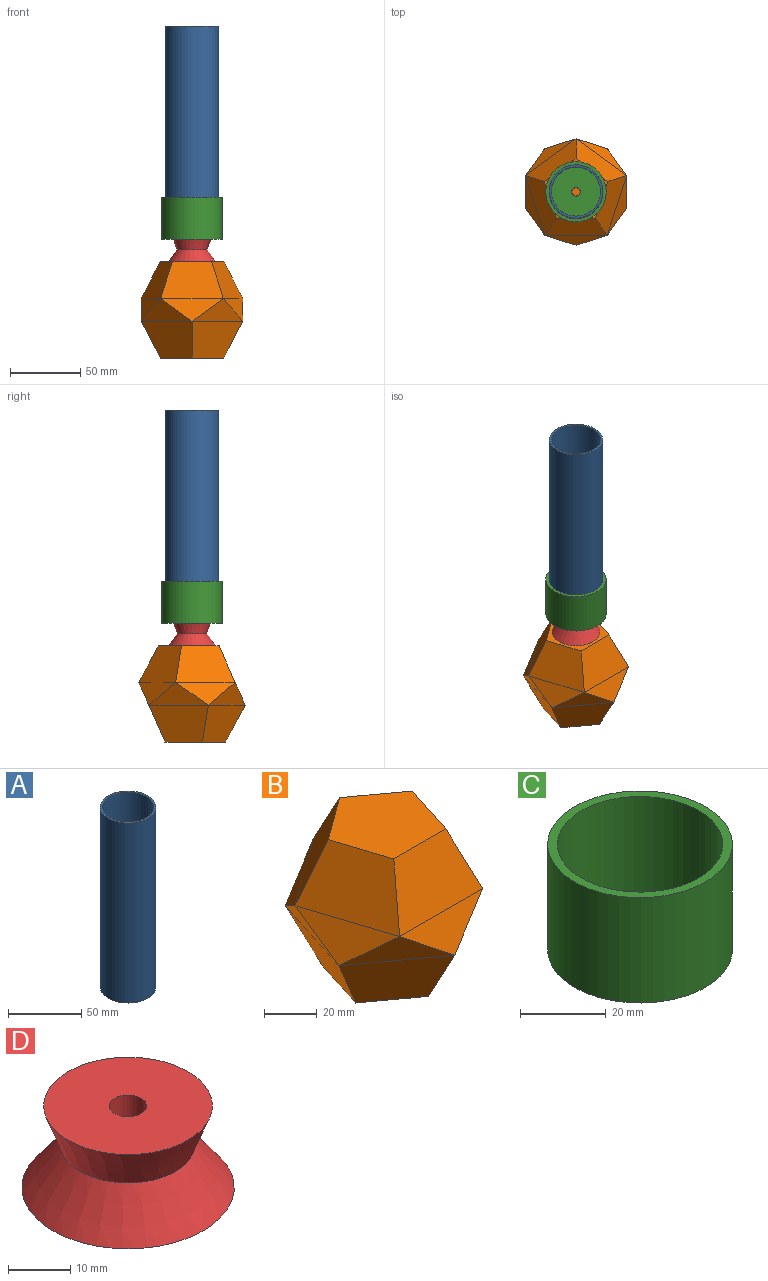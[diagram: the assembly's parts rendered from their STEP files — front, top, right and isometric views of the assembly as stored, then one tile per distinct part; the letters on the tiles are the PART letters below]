
ASSEMBLY  parts=4 mates=3
PART A: 4 faces, bbox 38x38x150 mm
  f0: cylinder r=17.5mm len=150mm, axis (0,0,-1), area 16493.4mm2, adj f2,f3
  f1: cylinder r=19mm len=150mm, axis (0,0,-1), area 17907.1mm2, adj f2,f3
  f2: plane 38x38mm, normal (0,0,1), area 172mm2, adj f0,f1
  f3: plane 38x38mm, normal (0,0,-1), area 172mm2, adj f0,f1
PART B: 22 faces, bbox 72.3x76x68.7 mm
  f0: plane 45.31x43.09mm, normal (0,0,1), area 1348.9mm2, adj f1,f2,f3,f4,f5
  f1: plane 44.66x26.25mm, normal (0,-0.92,0.4), area 1040.6mm2, adj f0,f2,f5,f7
  f2: plane 42.47x26.25mm, normal (0.87,-0.28,0.4), area 1040.6mm2, adj f0,f1,f3,f8
  f3: plane 36.13x30.63mm, normal (0.54,0.74,0.4), area 1040.6mm2, adj f0,f2,f4,f9
  f4: plane 36.13x30.63mm, normal (-0.54,0.74,0.4), area 1040.6mm2, adj f0,f3,f5,f10
  f5: plane 42.47x26.25mm, normal (-0.87,-0.28,0.4), area 1040.6mm2, adj f0,f1,f4,f6
  f6: plane 42.47x16.22mm, normal (-0.87,-0.28,0.41), area 396.8mm2, adj f5,f14,f15
  f7: plane 44.66x16.22mm, normal (0,-0.91,0.41), area 396.8mm2, adj f1,f11,f15
  f8: plane 42.47x16.22mm, normal (0.87,-0.28,0.41), area 396.8mm2, adj f2,f11,f12
  f9: plane 36.13x26.25mm, normal (0.54,0.74,0.41), area 396.8mm2, adj f3,f12,f13
  f10: plane 36.13x26.25mm, normal (-0.54,0.74,0.41), area 396.8mm2, adj f4,f13,f14
  f11: plane 36.13x26.25mm, normal (0.54,-0.74,-0.41), area 396.8mm2, adj f7,f8,f19
  f12: plane 42.47x16.22mm, normal (0.87,0.28,-0.41), area 396.8mm2, adj f8,f9,f18
  f13: plane 44.66x16.22mm, normal (0,0.91,-0.41), area 396.8mm2, adj f9,f10,f17
  f14: plane 42.47x16.22mm, normal (-0.87,0.28,-0.41), area 396.8mm2, adj f6,f10,f21
  f15: plane 36.13x26.25mm, normal (-0.54,-0.74,-0.41), area 396.8mm2, adj f6,f7,f20
  f16: plane 45.31x43.09mm, normal (0,0,-1), area 1348.9mm2, adj f17,f18,f19,f20,f21
  f17: plane 44.66x26.25mm, normal (0,0.92,-0.4), area 1040.6mm2, adj f13,f16,f18,f21
  f18: plane 42.47x26.25mm, normal (0.87,0.28,-0.4), area 1040.6mm2, adj f12,f16,f17,f19
  f19: plane 36.13x30.63mm, normal (0.54,-0.74,-0.4), area 1040.6mm2, adj f11,f16,f18,f20
  f20: plane 36.13x30.63mm, normal (-0.54,-0.74,-0.4), area 1040.6mm2, adj f15,f16,f19,f21
  f21: plane 42.47x26.25mm, normal (-0.87,0.28,-0.4), area 1040.6mm2, adj f14,f16,f17,f20
PART C: 6 faces, bbox 43x43x30 mm
  f0: plane 38.5x38.5mm, normal (0,0,1), area 1135.9mm2, adj f1,f4
  f1: cylinder r=3mm len=6mm, axis (0,0,-1), area 37.7mm2, adj f0,f3
  f2: cylinder r=21.5mm len=43mm, axis (0,0,-1), area 4052.7mm2, adj f3,f5
  f3: plane 43x43mm, normal (0,0,-1), area 1423.9mm2, adj f1,f2
  f4: cylinder r=19.25mm len=38.5mm, axis (0,0,-1), area 3386.6mm2, adj f0,f5
  f5: plane 43x43mm, normal (0,0,1), area 288mm2, adj f2,f4
PART D: 5 faces, bbox 34x34x16 mm
  f0: plane 34x34mm, normal (0,0,-1), area 879.6mm2, adj f1,f4
  f1: cone r=11mm half-angle=36.9deg, axis (0,0,-1), area 917.5mm2, adj f0,f3
  f2: plane 27x27mm, normal (0,0,1), area 544.3mm2, adj f3,f4
  f3: cone r=13.5mm half-angle=20.6deg, axis (0,0,1), area 612.6mm2, adj f1,f2
  f4: cylinder r=3mm len=16mm, axis (0,0,-1), area 301.6mm2, adj f0,f2
PLACE A t=(45.17,85.11,96.55)mm
PLACE B t=(45.17,85.11,11.83)mm
PLACE C t=(45.17,85.11,96.55)mm
PLACE D t=(45.17,85.11,80.55)mm
MATE fastened A.f0 <-> C.f1  axis (0,0,-1) through (45.17,85.11,98.55)mm
MATE fastened C.f1 <-> D.f1  axis (0,0,-1) through (45.17,85.11,96.55)mm
MATE fastened B.f0 <-> D.f1  axis (0,0,1) through (45.17,85.11,80.55)mm
